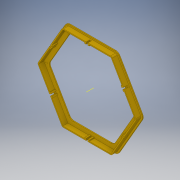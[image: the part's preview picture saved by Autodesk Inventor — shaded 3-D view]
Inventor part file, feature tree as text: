
AUTODESK INVENTOR PART (.ipt)
format: ipt  version: 2019 (Build 230136000, 136)  size: 573,440 bytes
history: native  units: mm
features: extrude x6, sketch x6, projected_geometry x3, fillet x2, other x1, pattern_circular x1
ambient origin geometry x8: Origin, YZ Plane, XZ Plane, XY Plane, X Axis, Y Axis, Z Axis, Center Point
bodies: Solid1 (feature_tree)
feature tree (19):
  extrude  "Extrusion1"  Depth=2.0mm
  extrude  "Extrusion5"  Depth=3.0mm
  extrude  "Extrusion6"  Depth=10.0mm
  fillet  "Fillet1"  [1 undecoded]
  fillet  "Fillet2"  Radius=8.0mm
  extrude  "Extrusion7"  TaperAngle=0.0deg  [1 undecoded]
  extrude  "Extrusion8"  Depth=4.0mm
  other  "Work Axis2"
  pattern_circular  "Circular Pattern1"  [2 undecoded]
  extrude  "Extrusion9"  Depth=7.5mm
  sketch  "Sketch1"  dims[d0=175.0mm d1=2.0mm]
  sketch  "Sketch5"  dims[d2=0.0mm d15=3.0mm]
  projected_geometry  "Projected Loop4"
  sketch  "Sketch7"  dims[d16=2.0mm d17=10.0mm d18=0.0mm d19=8.0mm]
  projected_geometry  "Projected Loop6"
  sketch  "Sketch8"  dims[d20=7.0mm d21=0.0mm]
  sketch  "Sketch9"  dims[d22=10.0mm d23=4.0mm]
  projected_geometry  "Projected Loop7"
  sketch  "Sketch11"  dims[d24=10.0mm d25=3.3mm d26=7.5mm d27=0.0mm d28=4.0mm d29=3.0mm d30=5.0mm d31=0.0mm d32=60.0mm d33=360.0deg d35=1.0mm d36=3.0mm d37=0.5mm d38=0.0mm]
note: 4 required parameter values undecoded (feature->parameter linkage not recoverable at this tier; creation-order binding heuristic only, values carry confidence <= 0.55)
